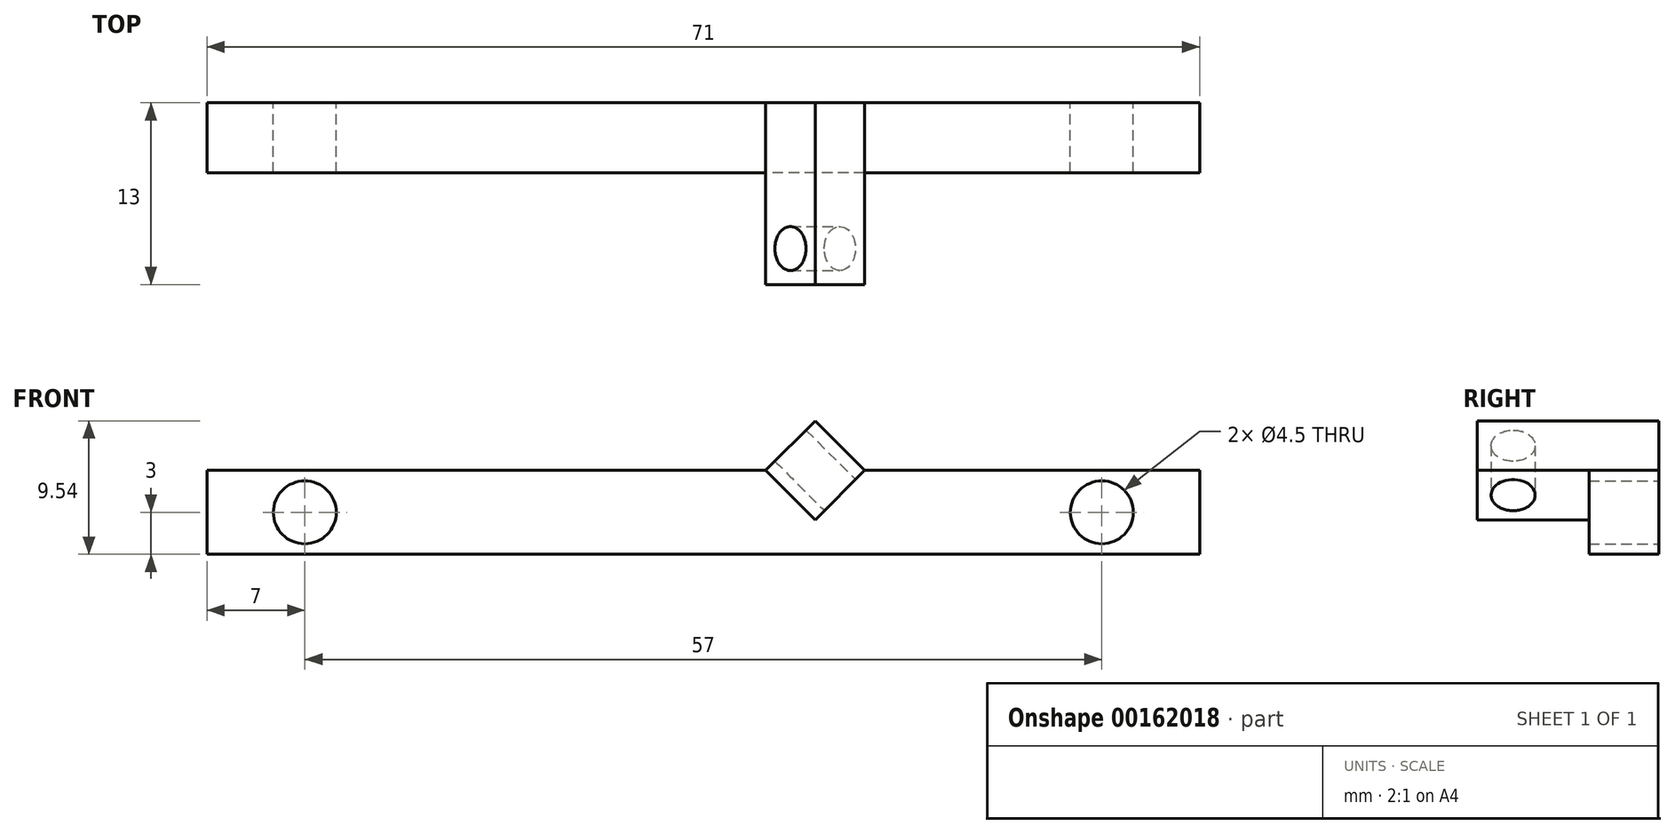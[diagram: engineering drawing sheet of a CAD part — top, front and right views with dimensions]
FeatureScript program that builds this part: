
annotation { "Feature Type Name" : "Feature", "Feature Type Description" : "" }
export const myFeature = defineFeature(function(context is Context, id is Id, definition is map)
    precondition{}
    {
        {
            var Q0;
            Q0=qCreatedBy(makeId("Front.planeOp"),FACE);
            var sketch = newSketch(context, id + "F0", { "sketchPlane" : qUnion([Q0])});
            skLineSegment(sketch, "E0.bottom", {"start": v(35.5, 3) * mm, "end": v(-35.5, 3) * mm});
            skLineSegment(sketch, "E0.top", {"start": v(35.5, -3) * mm, "end": v(-35.5, -3) * mm});
            skLineSegment(sketch, "E0.left", {"start": v(35.5, 3) * mm, "end": v(35.5, -3) * mm});
            skLineSegment(sketch, "E0.right", {"start": v(-35.5, 3) * mm, "end": v(-35.5, -3) * mm});
            skPoint(sketch, "E0.middle", {"position": v(0, 0) * mm});
            skCircle(sketch, "E1", {"center": v(-28.5, 0) * mm, "radius": 2.25 * mm});
            skPoint(sketch, "E1.centerSnap0", {"position": v(-35.5, 0) * mm});
            skLineSegment(sketch, "E2", {"start": v(0, 0) * mm, "end": v(0, 3) * mm, "construction": true});
            skCircle(sketch, "E3.MirrorC", {"center": v(28.5, 0) * mm, "radius": 2.25 * mm});
            skLineSegment(sketch, "E4", {"start": v(16.82, 17.68) * mm, "end": v(19.82, 20.68) * mm});
            skLineSegment(sketch, "E5", {"start": v(4.46, 3) * mm, "end": v(8, 6.54) * mm});
            skLineSegment(sketch, "E6", {"start": v(11.54, 3) * mm, "end": v(8, -0.54) * mm});
            skLineSegment(sketch, "E7", {"start": v(4.46, 3) * mm, "end": v(8, -0.54) * mm});
            skLineSegment(sketch, "E8", {"start": v(8, 6.54) * mm, "end": v(11.54, 3) * mm});
            skSolve(sketch);
        }
        {
            var Q0;
            Q0=qSketchRegion(id+"F0",true);
            extrude(context, id + "F1", {"entities" : qUnion([Q0]), "depth" : 5 * mm});
        }
        {
            var Q0;
            Q0=makeQuery(id+"F1.opExtrude","CAP_FACE",FACE,{"disambiguationData":[OSD([sQuery(id+"F0.wireOp",EDGE,"E0.bottom"),sQuery(id+"F0.wireOp",EDGE,"E0.top"),sQuery(id+"F0.wireOp",EDGE,"E0.left"),sQuery(id+"F0.wireOp",EDGE,"E0.right"),sQuery(id+"F0.wireOp",EDGE,"E1"),sQuery(id+"F0.wireOp",EDGE,"E3.MirrorC"),sQuery(id+"F0.wireOp",EDGE,"E5"),sQuery(id+"F0.wireOp",EDGE,"E8")])],"isStart":false});
            var sketch = newSketch(context, id + "F2", { "sketchPlane" : qUnion([Q0])});
            skLineSegment(sketch, "E9", {"start": v(8, 6.54) * mm, "end": v(4.46, 3) * mm});
            skLineSegment(sketch, "E10", {"start": v(8, 6.54) * mm, "end": v(11.54, 3) * mm});
            skLineSegment(sketch, "E11", {"start": v(11.54, 3) * mm, "end": v(8, -0.54) * mm});
            skLineSegment(sketch, "E12", {"start": v(8, -0.54) * mm, "end": v(4.46, 3) * mm});
            skSolve(sketch);
        }
        {
            var Q0;
            Q0=qSketchRegion(id+"F2",true);
            extrude(context, id + "F3", {"entities" : qUnion([Q0]), "operationType" : NewBodyOperationType.ADD, "depth" : 8 * mm});
        }
        {
            var Q0;
            Q0=makeQuery(id+"F3.opExtrude","SWEPT_FACE",FACE,{"disambiguationData":[OSD([sQuery(id+"F2.wireOp",EDGE,"E11")])]});
            var sketch = newSketch(context, id + "F4", { "sketchPlane" : qUnion([Q0])});
            skPoint(sketch, "E13.centerSnap0", {"position": v(-13, 7.78) * mm});
            skCircle(sketch, "E14", {"center": v(-10.43, 7.78) * mm, "radius": 1.57 * mm});
            skSolve(sketch);
        }
        {
            var Q0;
            Q0=qSketchRegion(id+"F4",true);
            extrude(context, id + "F5", {"entities" : qUnion([Q0]), "operationType" : NewBodyOperationType.REMOVE, "endBound" : BoundingType.THROUGH_ALL, "oppositeDirection" : true, "depth" : 25 * mm});
        }
    });
